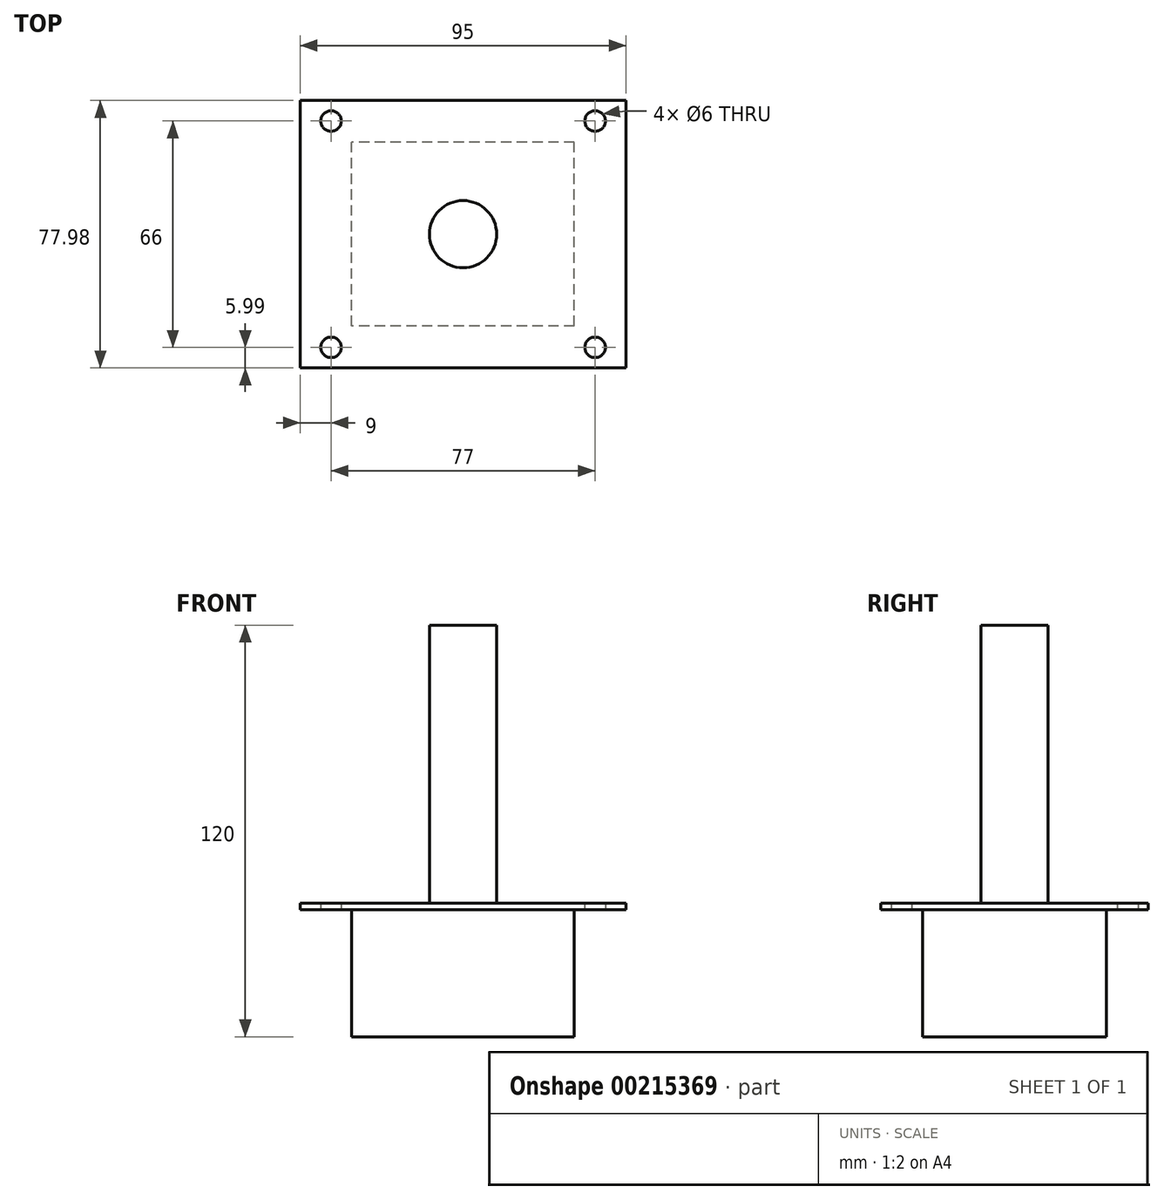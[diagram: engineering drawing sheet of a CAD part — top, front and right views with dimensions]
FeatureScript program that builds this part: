
annotation { "Feature Type Name" : "Feature", "Feature Type Description" : "" }
export const myFeature = defineFeature(function(context is Context, id is Id, definition is map)
    precondition{}
    {
        {
            var Q0;
            Q0=qCreatedBy(makeId("Top.planeOp"),FACE);
            var sketch = newSketch(context, id + "F0", { "sketchPlane" : qUnion([Q0])});
            skLineSegment(sketch, "E0.bottom", {"start": v(47.5, 38.99) * mm, "end": v(-47.5, 38.99) * mm});
            skLineSegment(sketch, "E0.top", {"start": v(47.5, -38.99) * mm, "end": v(-47.5, -38.99) * mm});
            skLineSegment(sketch, "E0.left", {"start": v(47.5, 38.99) * mm, "end": v(47.5, -38.99) * mm});
            skLineSegment(sketch, "E0.right", {"start": v(-47.5, 38.99) * mm, "end": v(-47.5, -38.99) * mm});
            skPoint(sketch, "E0.middle", {"position": v(0, 0) * mm});
            skLineSegment(sketch, "E1.bottom", {"start": v(38.5, 33) * mm, "end": v(-38.5, 33) * mm, "construction": true});
            skLineSegment(sketch, "E1.top", {"start": v(38.5, -33) * mm, "end": v(-38.5, -33) * mm, "construction": true});
            skLineSegment(sketch, "E1.left", {"start": v(38.5, 33) * mm, "end": v(38.5, -33) * mm, "construction": true});
            skLineSegment(sketch, "E1.right", {"start": v(-38.5, 33) * mm, "end": v(-38.5, -33) * mm, "construction": true});
            skCircle(sketch, "E2", {"center": v(38.5, 33) * mm, "radius": 3 * mm});
            skCircle(sketch, "E3", {"center": v(38.5, -33) * mm, "radius": 3 * mm});
            skCircle(sketch, "E4", {"center": v(-38.5, -33) * mm, "radius": 3 * mm});
            skCircle(sketch, "E5", {"center": v(-38.5, 33) * mm, "radius": 3 * mm});
            skSolve(sketch);
        }
        {
            var Q0;
            Q0 = qSketchRegion(id + "F0", true);
            extrude(context, id + "F1", {"entities" : qUnion([Q0]), "depth" : 2 * mm});
        }
        {
            var Q0;
            Q0=makeQuery(id+"F1.opExtrude","CAP_FACE",FACE,{"disambiguationData":[OSD([sQuery(id+"F0.wireOp",EDGE,"E0.bottom"),sQuery(id+"F0.wireOp",EDGE,"E0.top"),sQuery(id+"F0.wireOp",EDGE,"E0.left"),sQuery(id+"F0.wireOp",EDGE,"E0.right"),sQuery(id+"F0.wireOp",EDGE,"E2"),sQuery(id+"F0.wireOp",EDGE,"E3"),sQuery(id+"F0.wireOp",EDGE,"E4"),sQuery(id+"F0.wireOp",EDGE,"E5")])],"isStart":true});
            var sketch = newSketch(context, id + "F2", { "sketchPlane" : qUnion([Q0])});
            skLineSegment(sketch, "E6.bottom", {"start": v(32.44, 26.76) * mm, "end": v(-32.44, 26.76) * mm});
            skLineSegment(sketch, "E6.top", {"start": v(32.44, -26.76) * mm, "end": v(-32.44, -26.76) * mm});
            skLineSegment(sketch, "E6.left", {"start": v(32.44, 26.76) * mm, "end": v(32.44, -26.76) * mm});
            skLineSegment(sketch, "E6.right", {"start": v(-32.44, 26.76) * mm, "end": v(-32.44, -26.76) * mm});
            skPoint(sketch, "E6.middle", {"position": v(0, 0) * mm});
            skSolve(sketch);
        }
        {
            var Q0;
            Q0 = qSketchRegion(id + "F2", true);
            extrude(context, id + "F3", {"entities" : qUnion([Q0]), "operationType" : NewBodyOperationType.ADD, "depth" : 37 * mm});
        }
        {
            var Q0;
            Q0=makeQuery(id+"F1.opExtrude","CAP_FACE",FACE,{"disambiguationData":[OSD([sQuery(id+"F0.wireOp",EDGE,"E0.bottom"),sQuery(id+"F0.wireOp",EDGE,"E0.top"),sQuery(id+"F0.wireOp",EDGE,"E0.left"),sQuery(id+"F0.wireOp",EDGE,"E0.right"),sQuery(id+"F0.wireOp",EDGE,"E2"),sQuery(id+"F0.wireOp",EDGE,"E3"),sQuery(id+"F0.wireOp",EDGE,"E4"),sQuery(id+"F0.wireOp",EDGE,"E5")])],"isStart":false});
            var sketch = newSketch(context, id + "F4", { "sketchPlane" : qUnion([Q0])});
            skCircle(sketch, "E7", {"center": v(0, 0) * mm, "radius": 9.8 * mm});
            skSolve(sketch);
        }
        {
            var Q0;
            Q0 = qSketchRegion(id + "F4", true);
            extrude(context, id + "F5", {"entities" : qUnion([Q0]), "operationType" : NewBodyOperationType.ADD, "depth" : 81 * mm});
        }
    });
